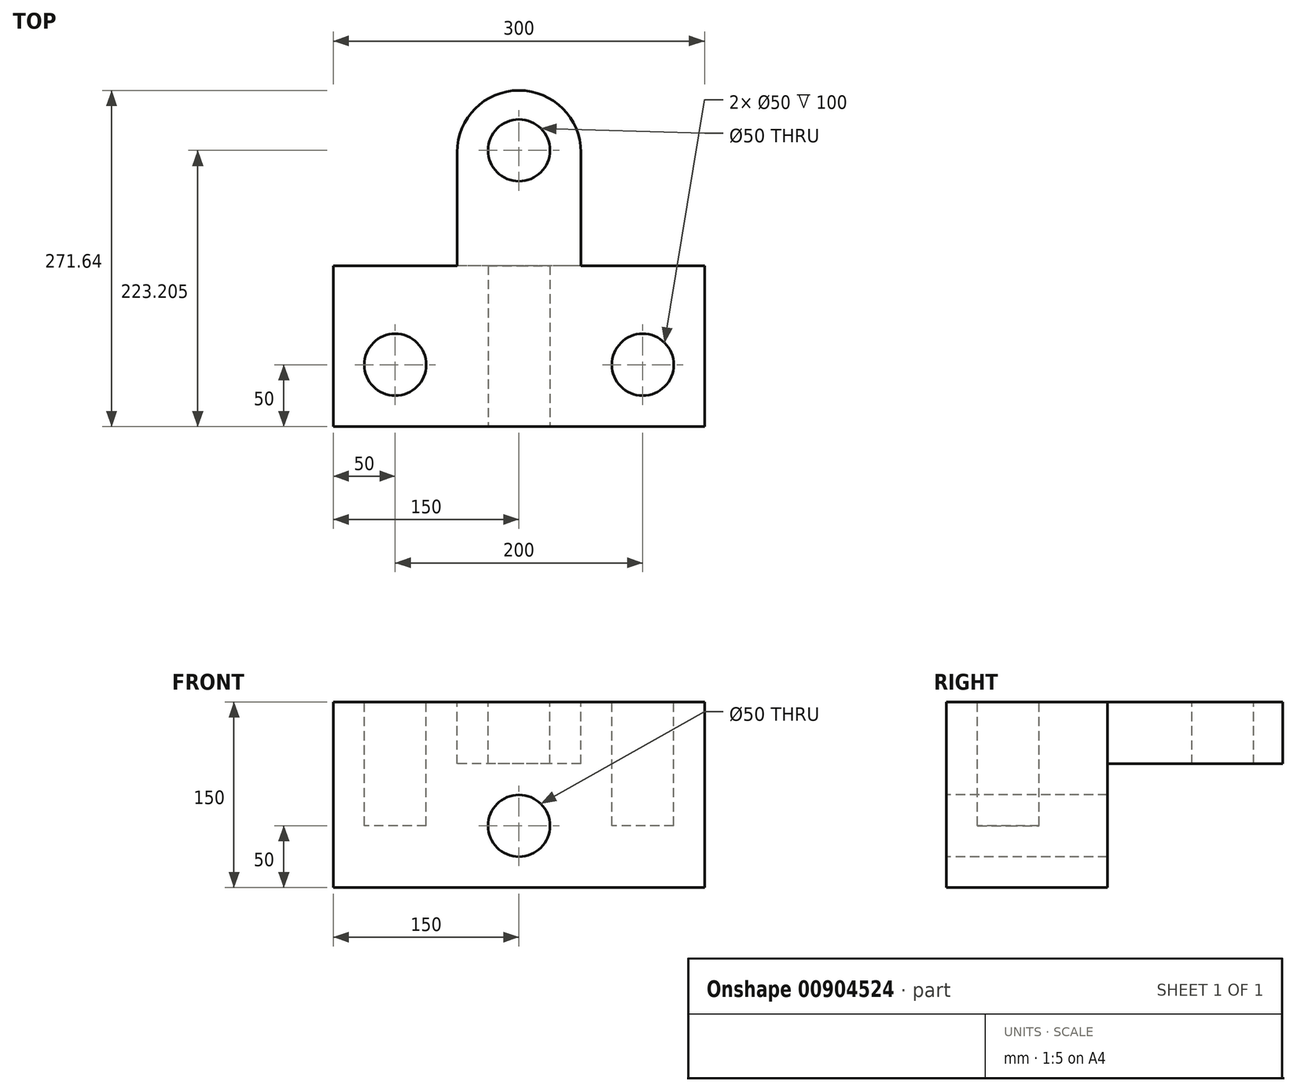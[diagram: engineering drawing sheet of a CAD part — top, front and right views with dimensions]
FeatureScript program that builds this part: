
annotation { "Feature Type Name" : "Feature", "Feature Type Description" : "" }
export const myFeature = defineFeature(function(context is Context, id is Id, definition is map)
    precondition{}
    {
        {
            var Q0;
            Q0=qCreatedBy(makeId("Front.planeOp"),FACE);
            var sketch = newSketch(context, id + "F0", { "sketchPlane" : qUnion([Q0])});
            skLineSegment(sketch, "E0.bottom", {"start": v(-80, 80) * mm, "end": v(80, 80) * mm});
            skLineSegment(sketch, "E0.top", {"start": v(-80, -80) * mm, "end": v(80, -80) * mm});
            skLineSegment(sketch, "E0.left", {"start": v(-80, 80) * mm, "end": v(-80, -80) * mm});
            skLineSegment(sketch, "E0.right", {"start": v(80, 80) * mm, "end": v(80, -80) * mm});
            skSolve(sketch);
        }
        {
            var Q0;
            Q0=makeQuery(id+"F0.imprint","IMPRINT",FACE,{"disambiguationData":[TD([[makeQuery(id+"F0.imprint","IMPRINT",EDGE,{"derivedFrom":sQuery(id+"F0.wireOp",EDGE,"E0.bottom")}),-1.0]])]});
            extrude(context, id + "F1", {"entities" : qUnion([Q0]), "depth" : 160 * mm, "offsetDistance" : 25 * mm});
        }
        {
            var Q0;
            Q0=makeQuery(id+"F1.opExtrude","CAP_FACE",FACE,{"disambiguationData":[OSD([sQuery(id+"F0.wireOp",EDGE,"E0.bottom"),sQuery(id+"F0.wireOp",EDGE,"E0.top"),sQuery(id+"F0.wireOp",EDGE,"E0.left"),sQuery(id+"F0.wireOp",EDGE,"E0.right")])],"isStart":true});
            var sketch = newSketch(context, id + "F2", { "sketchPlane" : qUnion([Q0])});
            skSolve(sketch);
        }
        {
            var Q0;
            Q0=makeQuery(id+"F1.opExtrude","SWEPT_BODY",BODY,{"disambiguationData":[OSD([sQuery(id+"F0.wireOp",EDGE,"E0.bottom"),sQuery(id+"F0.wireOp",EDGE,"E0.top"),sQuery(id+"F0.wireOp",EDGE,"E0.left"),sQuery(id+"F0.wireOp",EDGE,"E0.right")])]});
            deleteBodies(context, id + "F3", {"entities" : qUnion([Q0])});
        }
        {
            var Q0;
            Q0=makeQuery(id+"F2.imprint","IMPRINT",FACE,{"disambiguationData":[TD([[makeQuery(id+"F2.imprint","IMPRINT",EDGE,{"derivedFrom":makeQuery(id+"F1.opExtrude","CAP_EDGE",EDGE,{"disambiguationData":[OSD([sQuery(id+"F0.wireOp",EDGE,"E0.bottom")])],"isStart":true})}),1.0]])]});
            var sketch = newSketch(context, id + "F4", { "sketchPlane" : qUnion([Q0])});
            skLineSegment(sketch, "E1.bottom", {"start": v(-150, 75) * mm, "end": v(150, 75) * mm});
            skLineSegment(sketch, "E1.top", {"start": v(-150, -75) * mm, "end": v(150, -75) * mm});
            skLineSegment(sketch, "E1.left", {"start": v(-150, 75) * mm, "end": v(-150, -75) * mm});
            skLineSegment(sketch, "E1.right", {"start": v(150, 75) * mm, "end": v(150, -75) * mm});
            skSolve(sketch);
        }
        {
            var Q0;
            {var subQ0=sQuery(id+"F4.wireOp",EDGE,"E1.bottom");var subQ1=makeQuery(id+"F2.imprint","IMPRINT",EDGE,{"derivedFrom":makeQuery(id+"F1.opExtrude","CAP_EDGE",EDGE,{"disambiguationData":[OSD([sQuery(id+"F0.wireOp",EDGE,"E0.right")])],"isStart":true})});var subQ2=makeQuery(id+"F4.imprint","INTERSECT",VERTEX,{"derivedFrom":[subQ1,subQ0]});Q0=makeQuery(id+"F4.imprint","IMPRINT",FACE,{"disambiguationData":[TD([[makeQuery(id+"F4.imprint","IMPRINT",EDGE,{"disambiguationData":[TD([[subQ2,-1.0]])],"derivedFrom":subQ0}),-1.0]])]});}
            var Q1;
            {var subQ0=sQuery(id+"F4.wireOp",EDGE,"E1.left");Q1=makeQuery(id+"F4.imprint","IMPRINT",FACE,{"disambiguationData":[TD([[makeQuery(id+"F4.imprint","IMPRINT",EDGE,{"derivedFrom":subQ0}),1.0]])]});}
            var Q2;
            {var subQ0=sQuery(id+"F4.wireOp",EDGE,"E1.right");Q2=makeQuery(id+"F4.imprint","IMPRINT",FACE,{"disambiguationData":[TD([[makeQuery(id+"F4.imprint","IMPRINT",EDGE,{"derivedFrom":subQ0}),-1.0]])]});}
            extrude(context, id + "F5", {"entities" : qUnion([Q0, Q1, Q2]), "depth" : 130 * mm, "offsetDistance" : 25 * mm});
        }
        {
            var Q0;
            Q0=makeQuery(id+"F5.opExtrude","SWEPT_FACE",FACE,{"disambiguationData":[OSD([sQuery(id+"F4.wireOp",EDGE,"E1.bottom")])]});
            var sketch = newSketch(context, id + "F6", { "sketchPlane" : qUnion([Q0])});
            skLineSegment(sketch, "E2.bottom", {"start": v(50, 130) * mm, "end": v(-50, 130) * mm});
            skLineSegment(sketch, "E2.top", {"start": v(50, 273) * mm, "end": v(-50, 273) * mm});
            skLineSegment(sketch, "E2.left", {"start": v(50, 130) * mm, "end": v(50, 273) * mm});
            skLineSegment(sketch, "E2.right", {"start": v(-50, 130) * mm, "end": v(-50, 273) * mm});
            skSolve(sketch);
        }
        {
            var Q0;
            Q0=makeQuery(id+"F6.imprint","IMPRINT",FACE,{"disambiguationData":[TD([[makeQuery(id+"F6.imprint","IMPRINT",EDGE,{"derivedFrom":sQuery(id+"F6.wireOp",EDGE,"E2.bottom")}),-1.0]])]});
            extrude(context, id + "F7", {"entities" : qUnion([Q0]), "operationType" : NewBodyOperationType.ADD, "oppositeDirection" : true, "depth" : 50 * mm, "offsetDistance" : 25 * mm});
        }
        {
            var Q0;
            Q0=makeQuery(id+"F7.boolean.opBoolean","MERGE",FACE,{"derivedFrom":[makeQuery(id+"F5.opExtrude","SWEPT_FACE",FACE,{"disambiguationData":[OSD([sQuery(id+"F4.wireOp",EDGE,"E1.bottom")])]}),makeQuery(id+"F7.opExtrude","CAP_FACE",FACE,{"disambiguationData":[OSD([sQuery(id+"F6.wireOp",EDGE,"E2.bottom"),sQuery(id+"F6.wireOp",EDGE,"E2.top"),sQuery(id+"F6.wireOp",EDGE,"E2.left"),sQuery(id+"F6.wireOp",EDGE,"E2.right")])],"isStart":true})]});
            var sketch = newSketch(context, id + "F8", { "sketchPlane" : qUnion([Q0])});
            skCircle(sketch, "E3", {"center": v(100, 50) * mm, "radius": 25 * mm});
            skCircle(sketch, "E4", {"center": v(-100, 50) * mm, "radius": 25 * mm});
            skSolve(sketch);
        }
        {
            var Q0;
            Q0=makeQuery(id+"F8.imprint","IMPRINT",FACE,{"disambiguationData":[TD([[makeQuery(id+"F8.imprint","IMPRINT",EDGE,{"derivedFrom":sQuery(id+"F8.wireOp",EDGE,"E3")}),1.0]])]});
            var Q1;
            Q1=makeQuery(id+"F8.imprint","IMPRINT",FACE,{"disambiguationData":[TD([[makeQuery(id+"F8.imprint","IMPRINT",EDGE,{"derivedFrom":sQuery(id+"F8.wireOp",EDGE,"E4")}),1.0]])]});
            extrude(context, id + "F9", {"entities" : qUnion([Q0, Q1]), "operationType" : NewBodyOperationType.REMOVE, "oppositeDirection" : true, "depth" : 100 * mm, "offsetDistance" : 25 * mm});
        }
        {
            var Q0;
            Q0=makeQuery(id+"F7.boolean.opBoolean","MERGE",FACE,{"derivedFrom":[makeQuery(id+"F5.opExtrude","SWEPT_FACE",FACE,{"disambiguationData":[OSD([sQuery(id+"F4.wireOp",EDGE,"E1.bottom")])]}),makeQuery(id+"F7.opExtrude","CAP_FACE",FACE,{"disambiguationData":[OSD([sQuery(id+"F6.wireOp",EDGE,"E2.bottom"),sQuery(id+"F6.wireOp",EDGE,"E2.top"),sQuery(id+"F6.wireOp",EDGE,"E2.left"),sQuery(id+"F6.wireOp",EDGE,"E2.right")])],"isStart":true})]});
            var sketch = newSketch(context, id + "F10", { "sketchPlane" : qUnion([Q0])});
            skCircle(sketch, "E5", {"center": v(0, 223.2) * mm, "radius": 25 * mm});
            skSolve(sketch);
        }
        {
            var Q0;
            Q0=makeQuery(id+"F10.imprint","IMPRINT",FACE,{"disambiguationData":[TD([[makeQuery(id+"F10.imprint","IMPRINT",EDGE,{"derivedFrom":sQuery(id+"F10.wireOp",EDGE,"E5")}),1.0]])]});
            extrude(context, id + "F11", {"entities" : qUnion([Q0]), "operationType" : NewBodyOperationType.REMOVE, "oppositeDirection" : true, "depth" : 50 * mm, "offsetDistance" : 25 * mm});
        }
        {
            var Q0;
            Q0=makeQuery(id+"F7.boolean.opBoolean","MERGE",FACE,{"derivedFrom":[makeQuery(id+"F5.opExtrude","SWEPT_FACE",FACE,{"disambiguationData":[OSD([sQuery(id+"F4.wireOp",EDGE,"E1.bottom")])]}),makeQuery(id+"F7.opExtrude","CAP_FACE",FACE,{"disambiguationData":[OSD([sQuery(id+"F6.wireOp",EDGE,"E2.bottom"),sQuery(id+"F6.wireOp",EDGE,"E2.top"),sQuery(id+"F6.wireOp",EDGE,"E2.left"),sQuery(id+"F6.wireOp",EDGE,"E2.right")])],"isStart":true})]});
            var sketch = newSketch(context, id + "F12", { "sketchPlane" : qUnion([Q0])});
            skLineSegment(sketch, "E6", {"start": v(50, 221.64) * mm, "end": v(0, 221.64) * mm});
            skLineSegment(sketch, "E7", {"start": v(0, 221.64) * mm, "end": v(-50, 221.64) * mm});
            skLineSegment(sketch, "E8", {"start": v(0, 221.64) * mm, "end": v(0, 171.64) * mm});
            skArc(sketch, "E9", {"start": v(0, 171.64) * mm, "mid": v(35.36, 257) * mm, "end": v(-50, 221.64) * mm});
            skSolve(sketch);
        }
        {
            var Q0;
            {var subQ5=makeQuery(id+"F7.opExtrude","CAP_EDGE",EDGE,{"disambiguationData":[OSD([sQuery(id+"F6.wireOp",EDGE,"E2.top")])],"isStart":true});Q0=makeQuery(id+"F12.imprint","IMPRINT",FACE,{"disambiguationData":[TD([[makeQuery(id+"F12.imprint","IMPRINT",EDGE,{"derivedFrom":subQ5}),1.0]])]});}
            extrude(context, id + "F13", {"entities" : qUnion([Q0]), "operationType" : NewBodyOperationType.REMOVE, "oppositeDirection" : true, "depth" : 50 * mm, "offsetDistance" : 25 * mm});
        }
        {
            var Q0;
            Q0=makeQuery(id+"F5.opExtrude","CAP_FACE",FACE,{"disambiguationData":[OSD([sQuery(id+"F4.wireOp",EDGE,"E1.bottom"),sQuery(id+"F4.wireOp",EDGE,"E1.top"),sQuery(id+"F4.wireOp",EDGE,"E1.left"),sQuery(id+"F4.wireOp",EDGE,"E1.right")])],"isStart":true});
            var sketch = newSketch(context, id + "F14", { "sketchPlane" : qUnion([Q0])});
            skCircle(sketch, "E10", {"center": v(0, -25) * mm, "radius": 25 * mm});
            skSolve(sketch);
        }
        {
            var Q0;
            Q0=makeQuery(id+"F14.imprint","IMPRINT",FACE,{"disambiguationData":[TD([[makeQuery(id+"F14.imprint","IMPRINT",EDGE,{"derivedFrom":sQuery(id+"F14.wireOp",EDGE,"E10")}),1.0]])]});
            extrude(context, id + "F15", {"entities" : qUnion([Q0]), "operationType" : NewBodyOperationType.REMOVE, "oppositeDirection" : true, "depth" : 130 * mm, "offsetDistance" : 25 * mm});
        }
    });
